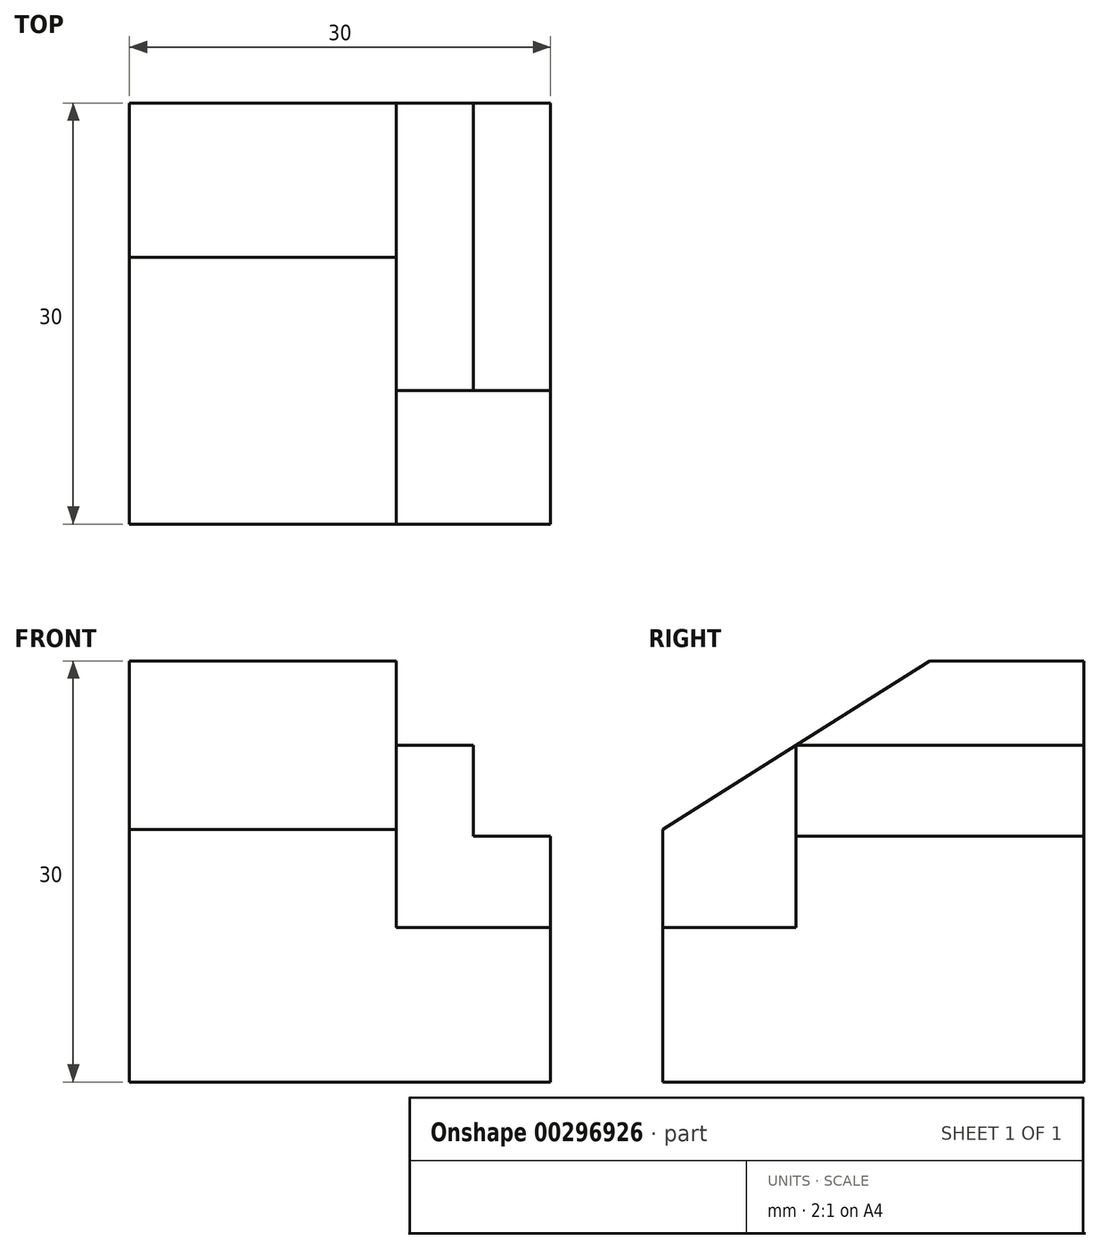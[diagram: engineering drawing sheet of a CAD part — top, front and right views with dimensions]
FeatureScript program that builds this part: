
annotation { "Feature Type Name" : "Feature", "Feature Type Description" : "" }
export const myFeature = defineFeature(function(context is Context, id is Id, definition is map)
    precondition{}
    {
        {
            var Q0;
            Q0=qCreatedBy(makeId("Right.planeOp"),FACE);
            var sketch = newSketch(context, id + "F0", { "sketchPlane" : qUnion([Q0])});
            skLineSegment(sketch, "E0.bottom", {"start": v(0, 0) * mm, "end": v(30, 0) * mm});
            skLineSegment(sketch, "E0.top", {"start": v(0, 30) * mm, "end": v(30, 30) * mm});
            skLineSegment(sketch, "E0.left", {"start": v(0, 0) * mm, "end": v(0, 30) * mm});
            skLineSegment(sketch, "E0.right", {"start": v(30, 0) * mm, "end": v(30, 30) * mm});
            skLineSegment(sketch, "E1", {"start": v(19, 30) * mm, "end": v(0, 18) * mm});
            skLineSegment(sketch, "E2", {"start": v(9.5, 24) * mm, "end": v(30, 24) * mm});
            skLineSegment(sketch, "E3", {"start": v(9.5, 24) * mm, "end": v(9.5, 11) * mm});
            skLineSegment(sketch, "E4", {"start": v(9.5, 11) * mm, "end": v(0, 11) * mm});
            skLineSegment(sketch, "E5", {"start": v(9.5, 17.5) * mm, "end": v(30, 17.5) * mm});
            skSolve(sketch);
        }
        {
            var Q0;
            {var subQ1=sQuery(id+"F0.wireOp",EDGE,"E0.bottom");Q0=makeQuery(id+"F0.imprint","IMPRINT",FACE,{"disambiguationData":[TD([[makeQuery(id+"F0.imprint","IMPRINT",EDGE,{"derivedFrom":subQ1}),1.0]])]});}
            var Q1;
            {var subQ0=sQuery(id+"F0.wireOp",EDGE,"E2");Q1=makeQuery(id+"F0.imprint","IMPRINT",FACE,{"disambiguationData":[TD([[makeQuery(id+"F0.imprint","IMPRINT",EDGE,{"derivedFrom":subQ0}),-1.0]])]});}
            var Q2;
            {var subQ5=sQuery(id+"F0.wireOp",EDGE,"E2");Q2=makeQuery(id+"F0.imprint","IMPRINT",FACE,{"disambiguationData":[TD([[makeQuery(id+"F0.imprint","IMPRINT",EDGE,{"derivedFrom":subQ5}),1.0]])]});}
            var Q3;
            {var subQ0=sQuery(id+"F0.wireOp",EDGE,"E4");Q3=makeQuery(id+"F0.imprint","IMPRINT",FACE,{"disambiguationData":[TD([[makeQuery(id+"F0.imprint","IMPRINT",EDGE,{"derivedFrom":subQ0}),-1.0]])]});}
            extrude(context, id + "F1", {"entities" : qUnion([Q0, Q1, Q2, Q3]), "oppositeDirection" : true, "depth" : 30 * mm});
        }
        {
            var Q0;
            {var subQ5=sQuery(id+"F0.wireOp",EDGE,"E2");Q0=makeQuery(id+"F0.imprint","IMPRINT",FACE,{"disambiguationData":[TD([[makeQuery(id+"F0.imprint","IMPRINT",EDGE,{"derivedFrom":subQ5}),1.0]])]});}
            var Q1;
            {var subQ0=sQuery(id+"F0.wireOp",EDGE,"E4");Q1=makeQuery(id+"F0.imprint","IMPRINT",FACE,{"disambiguationData":[TD([[makeQuery(id+"F0.imprint","IMPRINT",EDGE,{"derivedFrom":subQ0}),-1.0]])]});}
            extrude(context, id + "F2", {"entities" : qUnion([Q0, Q1]), "operationType" : NewBodyOperationType.REMOVE, "oppositeDirection" : true, "depth" : 11 * mm});
        }
        {
            var Q0;
            {var subQ0=sQuery(id+"F0.wireOp",EDGE,"E2");Q0=makeQuery(id+"F0.imprint","IMPRINT",FACE,{"disambiguationData":[TD([[makeQuery(id+"F0.imprint","IMPRINT",EDGE,{"derivedFrom":subQ0}),-1.0]])]});}
            extrude(context, id + "F3", {"entities" : qUnion([Q0]), "operationType" : NewBodyOperationType.REMOVE, "oppositeDirection" : true, "depth" : (11 / 2) * mm});
        }
    });
